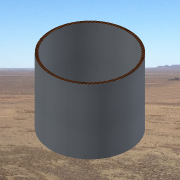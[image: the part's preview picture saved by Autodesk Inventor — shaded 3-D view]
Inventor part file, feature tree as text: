
AUTODESK INVENTOR PART (.ipt)
format: ipt  version: 2013 SP2 (Build 170200200, 200)  size: 133,120 bytes
history: native  units: in
note: dims shown in document units (in); Inventor stores cm internally (conversion verified against a paired STEP export)
features: extrude x1, sketch x1
ambient origin geometry x8: Origin, YZ Plane, XZ Plane, XY Plane, X Axis, Y Axis, Z Axis, Center Point
bodies: Solid1 (feature_tree)
feature tree (2):
  extrude  "Extrusion1"  Depth=0.375in
  sketch  "Sketch1"  dims[d0=12.0in d2=0.375in d3=10.0in d4=0.0in]
